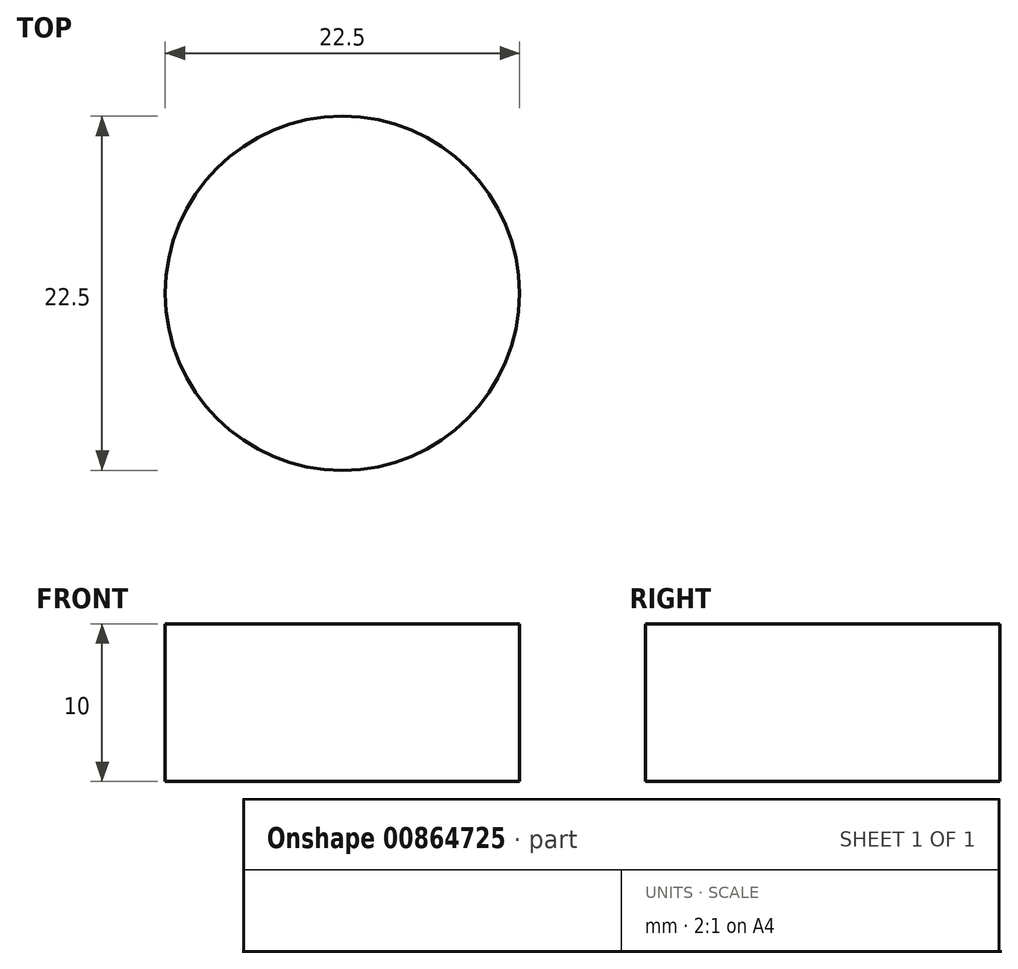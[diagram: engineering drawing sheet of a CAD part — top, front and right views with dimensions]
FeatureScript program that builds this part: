
annotation { "Feature Type Name" : "Feature", "Feature Type Description" : "" }
export const myFeature = defineFeature(function(context is Context, id is Id, definition is map)
    precondition{}
    {
        {
            var Q0;
            Q0=qCreatedBy(makeId("Top.planeOp"),FACE);
            var sketch = newSketch(context, id + "F0", { "sketchPlane" : qUnion([Q0])});
            skCircle(sketch, "E0", {"center": v(0, 0) * mm, "radius": 11.25 * mm});
            skCircle(sketch, "E1", {"center": v(0, 0) * mm, "radius": 8.75 * mm});
            skSolve(sketch);
        }
        {
            var Q0;
            Q0=sQuery(id+"F0.wireOp",EDGE,"E0");
            extrude(context, id + "F1", {"bodyType" : ToolBodyType.SURFACE, "surfaceEntities" : qUnion([Q0]), "depth" : 10 * mm, "offsetDistance" : 25.4 * mm});
        }
    });
